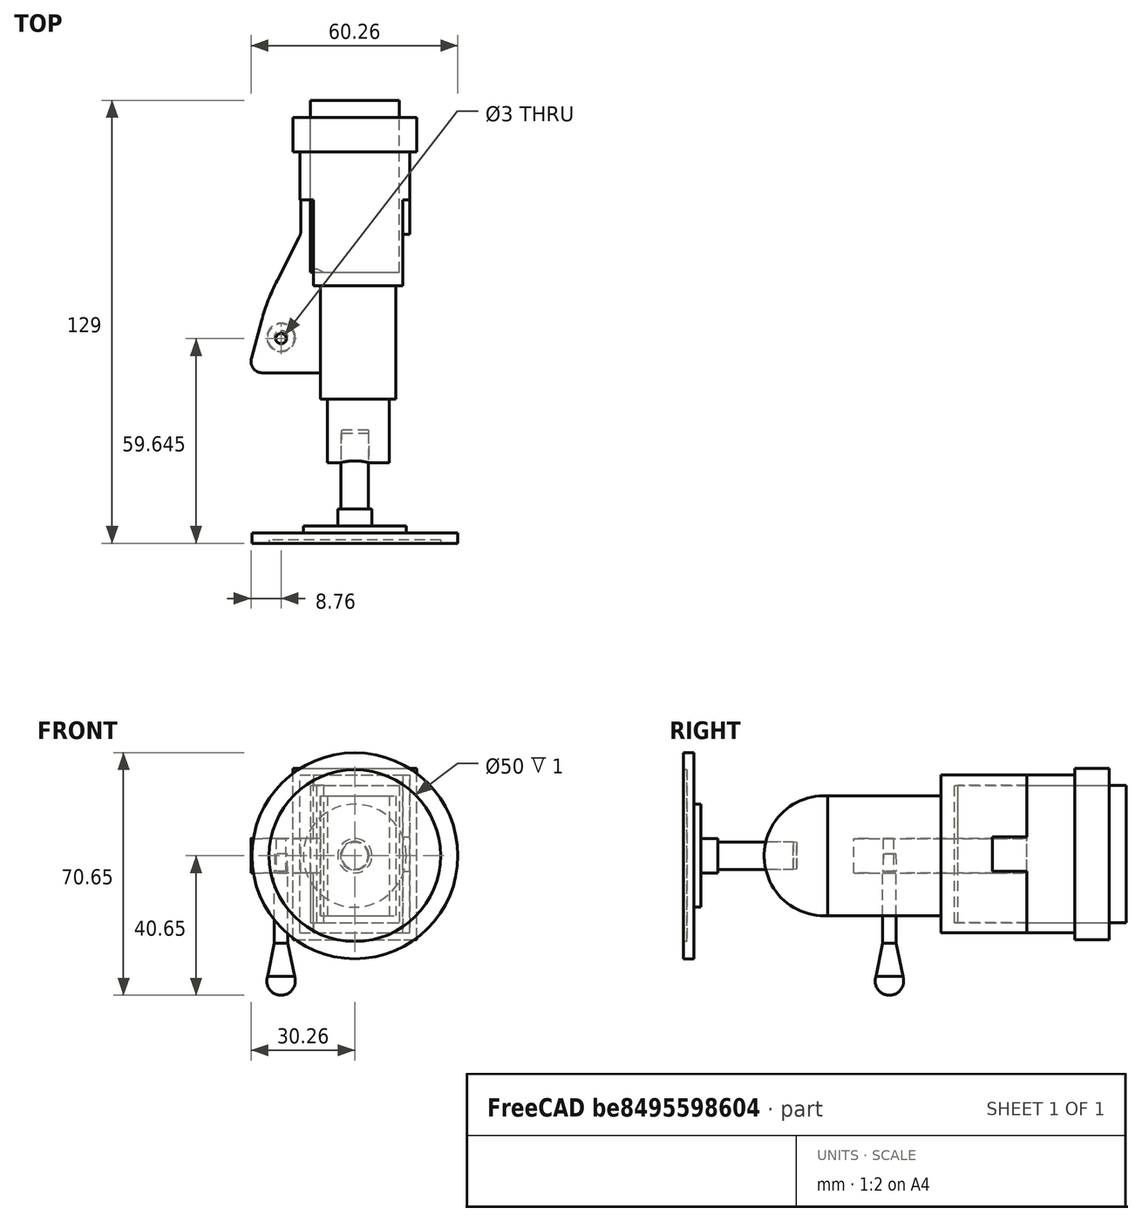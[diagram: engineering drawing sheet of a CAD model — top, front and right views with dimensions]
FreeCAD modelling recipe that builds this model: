
FCSTD DOCUMENT  (FreeCAD 0.16R6662 (Git))
Label: qtippholder-jw-rounded
License: All rights reserved
LicenseURL: http://en.wikipedia.org/wiki/All_rights_reserved
objects: Part::Cylinder×7, Part::Box×6, Part::Cone×3, Part::MultiFuse×3, Part::Cut×3, Sketcher::SketchObject×2, App::DocumentObjectGroup×2, Mesh::Feature×1, PartDesign::Pad×1, Part::Sphere×1, PartDesign::Pocket×1
note: 29 computed .brp shape members not serialized (recipe doc carries the construction recipe); baked Part::Feature solids carry a one-line shape summary decoded from their .brp

FEATURE [Mesh::Feature] EarClnrHldr
  Placement = pos=(1.7939,1.69608,-3.31283) rot=(0,0,1;0rad)
FEATURE [Part::Box] Box  label="hut"
  Height = 50
  Length = 36
  Placement = pos=(14,116,11) rot=(0,0,1;0rad)
  Width = 10
FEATURE [Part::Box] Box001  label="stirn"
  Height = 46
  Length = 32
  Placement = pos=(16,102,13) rot=(0,0,1;0rad)
  Width = 17
FEATURE [Part::Box] Box002  label="gnack"
  Height = 10
  Length = 26
  Placement = pos=(22,92,31) rot=(0,0,1;0rad)
  Width = 12
FEATURE [Part::Box] Box003  label="augen"
  Height = 46
  Length = 26
  Placement = pos=(20,77,13) rot=(0,0,1;0rad)
  Width = 26
FEATURE [Part::Box] Box004  label="wangen"
  Height = 35
  Length = 22
  Placement = pos=(22,44,18) rot=(0,0,1;0rad)
  Width = 36
FEATURE [Part::Cylinder] Cylinder  label="kinn"
  Angle = 360
  Height = 18
  Placement = pos=(24,43,35.5) rot=(0,1,0;1.5708rad)
  Radius = 17.5
FEATURE [Sketcher::SketchObject] Sketch001
  Placement = pos=(22,44,36) rot=(0,0,1;0rad)
  sketch-geometry (10):
    g0: LineSegment StartX=1.5 StartY=7.67084 StartZ=0 EndX=-16.9205 EndY=7.67084 EndZ=0
    g1: LineSegment StartX=-20.1462 StartY=11.8885 StartZ=0 EndX=-17.1712 EndY=22.8519 EndZ=0
    g2: LineSegment StartX=-12.6256 StartY=34.6 StartZ=0 EndX=-6.24014 EndY=47.0658 EndZ=0
    g3: LineSegment StartX=-5.70418 StartY=49.2877 StartZ=0 EndX=-5.70418 EndY=58.874 EndZ=0
    g4: LineSegment StartX=-5.70418 StartY=58.874 StartZ=0 EndX=1.5 EndY=58.874 EndZ=0
    g5: LineSegment StartX=1.5 StartY=58.874 StartZ=0 EndX=1.5 EndY=7.67084 EndZ=0
    g6: ArcOfCircle CenterX=-16.9205 CenterY=11.0132 CenterZ=0 NormalX=0 NormalY=0 NormalZ=1 Radius=3.34236 StartAngle=2.87662 EndAngle=4.71239
    g7: ArcOfCircle CenterX=41.2664 CenterY=6.99453 CenterZ=0 NormalX=0 NormalY=0 NormalZ=1 Radius=60.5508 StartAngle=2.6682 EndAngle=2.87662
    g8: ArcOfCircle CenterX=-10.5778 CenterY=49.2877 CenterZ=0 NormalX=0 NormalY=0 NormalZ=1 Radius=4.87365 StartAngle=5.8098 EndAngle=6.28319
    g9: Circle CenterX=-11.5 CenterY=17.6445 CenterZ=0 NormalX=0 NormalY=0 NormalZ=1 Radius=1.5
  constraints (14):
    c: Horizontal(g0)
    c: Vertical(g3)
    c: Coincident(g3,g4)
    c: Horizontal(g4)
    c: Coincident(g4,g5)
    c: Coincident(g5,g0)
    c: Vertical(g5)
    c: Tangent(g0,g6) = 1.5708
    c: Tangent(g1,g6) = 1.5708
    c: Tangent(g1,g7) = 1.5708
    c: Tangent(g2,g7) = 1.5708
    c: Tangent(g2,g8) = -1.5708
    c: Tangent(g3,g8) = -1.5708
    c: Radius(g9) = 1.5
FEATURE [PartDesign::Pad] Pad  label="nase"
  Length = 4.5
  Length2 = 5.5
  Placement = pos=(22,44,36) rot=(0,0,1;0rad)
  Sketch = -> Sketch001
  Type = 4
FEATURE [Part::Cylinder] Cylinder002  label="bein006"
  Angle = 360
  Height = 32
  Placement = pos=(32,34,35.5) rot=(1,0,0;1.5708rad)
  Radius = 4
FEATURE [Part::Cylinder] Cylinder003  label="bein001"
  Angle = 360
  Height = 11
  Placement = pos=(32,12,35.5) rot=(1,0,0;1.5708rad)
  Radius = 5
FEATURE [Part::Cylinder] Cylinder004  label="bein002"
  Angle = 360
  Height = 4
  Placement = pos=(32,7,35.5) rot=(1,0,0;1.5708rad)
  Radius = 15
FEATURE [Part::Cylinder] Cylinder005  label="bein003"
  Angle = 360
  Height = 3
  Placement = pos=(32,5,35.5) rot=(1,0,0;1.5708rad)
  Radius = 30
FEATURE [Part::Cylinder] Cylinder006  label="bein004"
  Angle = 360
  Height = 3
  Placement = pos=(32,3,35.5) rot=(1,0,0;1.5708rad)
  Radius = 25
FEATURE [Part::Box] Box005  label="kopfloch"
  Height = 40
  Length = 26
  Placement = pos=(19,81,16) rot=(0,0,1;0rad)
  Width = 50
FEATURE [Part::Cylinder] Cylinder007  label="staebchen"
  Angle = 360
  Height = 27
  Placement = pos=(10.5,62,4) rot=(0,0,1;0rad)
  Radius = 2
FEATURE [Part::Sphere] Sphere  label="Kugel"
  Angle1 = -90
  Angle2 = 90
  Angle3 = 360
  Placement = pos=(10.5,62,-1) rot=(0,0,1;0rad)
  Radius = 4.15
FEATURE [Part::Cone] Cone  label="Kegel"
  Angle = 360
  Height = 10
  Placement = pos=(10.5,62,0) rot=(0,0,1;0rad)
  Radius1 = 4
  Radius2 = 2
FEATURE [Part::Cone] Cone001  label="Kegel001"
  Angle = 360
  Height = 5
  Placement = pos=(10.5,62,31) rot=(0,0,1;0rad)
  Radius1 = 2
  Radius2 = 1.8
FEATURE [Part::Cone] Cone002  label="beinloch001"
  Angle = 360
  Height = 11
  Placement = pos=(32,35,35.5) rot=(1,0,0;1.5708rad)
  Radius1 = 3.9
  Radius2 = 4.2
FEATURE [Part::MultiFuse] Fusion
  Shapes = -> [Box,Box001,Box002,Box003,Box004,Cylinder,Pad]
FEATURE [Part::MultiFuse] Fusion001
  Shapes = -> [Cone001,Cylinder007,Sphere,Cone]
FEATURE [App::DocumentObjectGroup] Gruppe001  label="halb-qtipp"
  Group = -> [Fusion001]
FEATURE [Part::MultiFuse] Fusion002
  Shapes = -> [Cylinder002,Cylinder003,Cylinder005,Cylinder004]
FEATURE [Part::Cut] Cut002
  Base = -> Fusion002
  Tool = -> Cylinder006
FEATURE [App::DocumentObjectGroup] Gruppe  label="bein"
  Group = -> [Cut002]
FEATURE [Sketcher::SketchObject] Sketch
  Placement = pos=(19,81,16) rot=(1,0,0;3.14159rad)
  Support = -> Box005 [Face5]
  sketch-geometry (4):
    g0: LineSegment StartX=0 StartY=0 StartZ=0 EndX=0 EndY=-1 EndZ=0
    g1: LineSegment StartX=0 StartY=-1 StartZ=0 EndX=2 EndY=-1 EndZ=0
    g2: LineSegment StartX=2 StartY=-1 StartZ=0 EndX=4 EndY=0 EndZ=0
    g3: LineSegment StartX=4 StartY=0 StartZ=0 EndX=0 EndY=0 EndZ=0
  constraints (11):
    c: Coincident(g-1,g0)
    c: PointOnObject(g0,g-2)
    c: Coincident(g0,g1)
    c: Horizontal(g1)
    c: Coincident(g1,g2)
    c: Coincident(g2,g3)
    c: Coincident(g3,g0)
    c: Horizontal(g3)
    c: DistanceY(g0,g0) = 1
    c: DistanceX(g1,g1) = 2
    c: DistanceX(g3,g3) = 4
FEATURE [PartDesign::Pocket] Pocket
  Length = 5
  Placement = pos=(19,81,16) rot=(0,0,1;0rad)
  Sketch = -> Sketch
  Type = 1
FEATURE [Part::Cut] Cut
  Base = -> Fusion
  Tool = -> Pocket
FEATURE [Part::Cut] Cut003  label="kopf"
  Base = -> Cut
  Tool = -> Cone002
